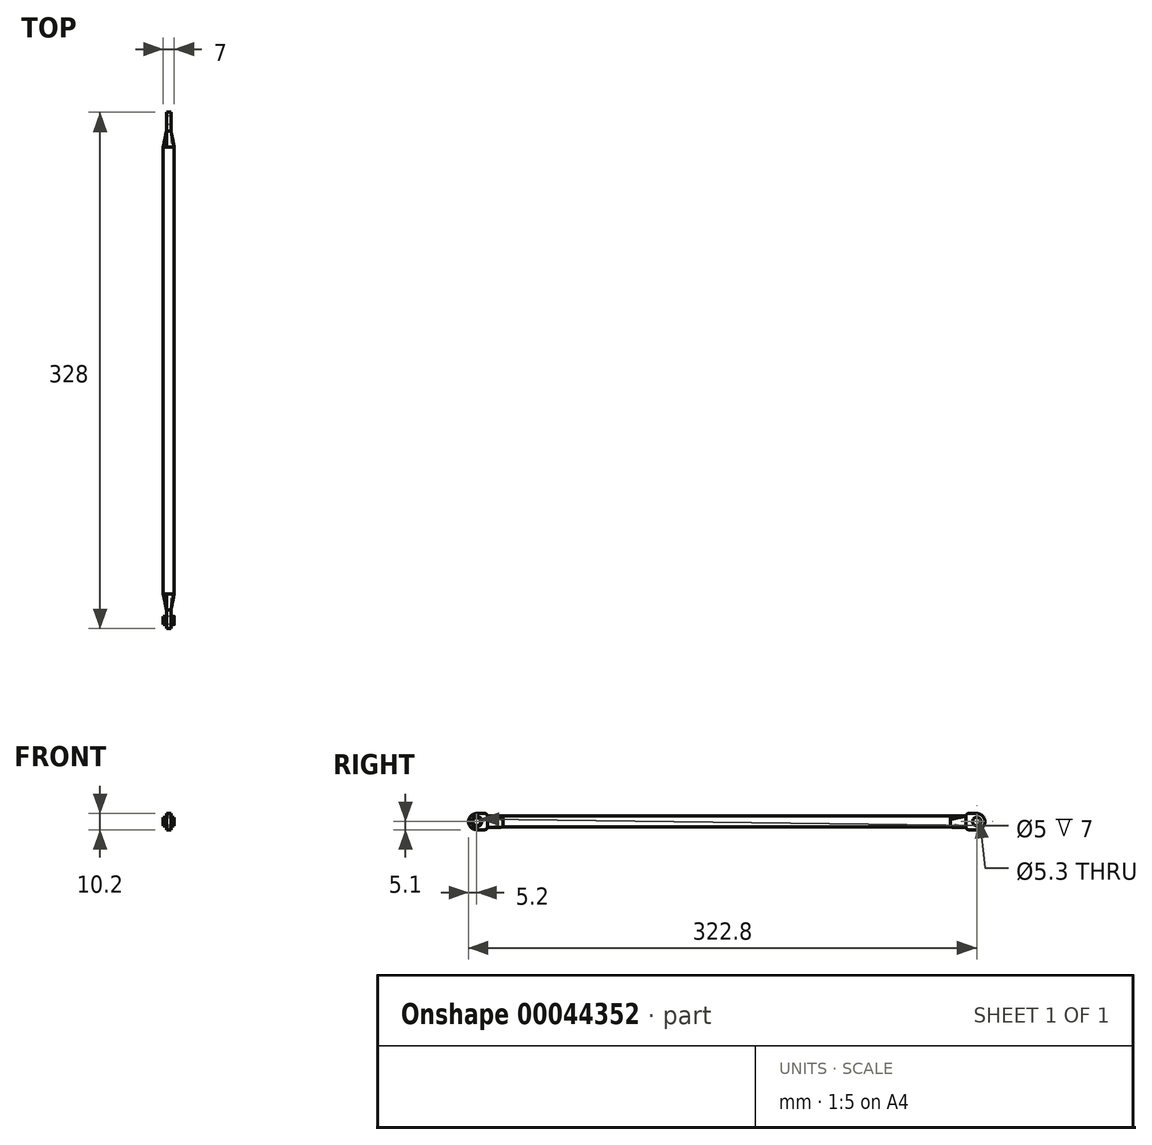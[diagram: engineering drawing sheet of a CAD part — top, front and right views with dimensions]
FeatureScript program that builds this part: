
annotation { "Feature Type Name" : "Feature", "Feature Type Description" : "" }
export const myFeature = defineFeature(function(context is Context, id is Id, definition is map)
    precondition{}
    {
        {
            var Q0;
            Q0=qCreatedBy(makeId("Right.planeOp"),FACE);
            var sketch = newSketch(context, id + "F0", { "sketchPlane" : qUnion([Q0])});
            skLineSegment(sketch, "E0.bottom", {"start": v(-0.9, 5.1) * mm, "end": v(4.5, 5.1) * mm});
            skLineSegment(sketch, "E0.top", {"start": v(-0.9, -5.1) * mm, "end": v(4.5, -5.1) * mm});
            skLineSegment(sketch, "E0.left", {"start": v(-6, 0) * mm, "end": v(-6, 0) * mm});
            skLineSegment(sketch, "E0.right", {"start": v(6, 3.6) * mm, "end": v(6, -3.6) * mm});
            skPoint(sketch, "E1.visualSharp", {"position": v(-6, 5.1) * mm});
            skArc(sketch, "E1.filletArc", {"start": v(-0.9, 5.1) * mm, "mid": v(-4.5, 3.6) * mm, "end": v(-6, 0) * mm});
            skPoint(sketch, "E2.visualSharp", {"position": v(-6, -5.1) * mm});
            skArc(sketch, "E2.filletArc", {"start": v(-6, 0) * mm, "mid": v(-4.5, -3.6) * mm, "end": v(-0.9, -5.1) * mm});
            skPoint(sketch, "E3.visualSharp", {"position": v(6, 5.1) * mm});
            skArc(sketch, "E3.filletArc", {"start": v(6, 3.6) * mm, "mid": v(5.56, 4.66) * mm, "end": v(4.5, 5.1) * mm});
            skPoint(sketch, "E4.visualSharp", {"position": v(6, -5.1) * mm});
            skArc(sketch, "E4.filletArc", {"start": v(4.5, -5.1) * mm, "mid": v(5.56, -4.66) * mm, "end": v(6, -3.6) * mm});
            skSolve(sketch);
        }
        {
            var Q0;
            Q0=makeQuery(id+"F0.imprint","IMPRINT",FACE,{"disambiguationData":[TD([[makeQuery(id+"F0.imprint","IMPRINT",EDGE,{"derivedFrom":sQuery(id+"F0.wireOp",EDGE,"E0.bottom")}),-1.0]])]});
            extrude(context, id + "F1", {"entities" : qUnion([Q0]), "endBound" : BoundingType.SYMMETRIC, "depth" : 3 * mm});
        }
        {
            var Q0;
            Q0=makeQuery(id+"F1.opExtrude","SWEPT_FACE",FACE,{"disambiguationData":[OSD([sQuery(id+"F0.wireOp",EDGE,"E0.right")])]});
            var sketch = newSketch(context, id + "F2", { "sketchPlane" : qUnion([Q0])});
            skLineSegment(sketch, "E5.bottom", {"start": v(-1.5, -3.6) * mm, "end": v(1.5, -3.6) * mm});
            skLineSegment(sketch, "E5.top", {"start": v(-1.5, 3.6) * mm, "end": v(1.5, 3.6) * mm});
            skLineSegment(sketch, "E5.left", {"start": v(-1.5, -3.6) * mm, "end": v(-1.5, 3.6) * mm});
            skLineSegment(sketch, "E5.right", {"start": v(1.5, -3.6) * mm, "end": v(1.5, 3.6) * mm});
            skSolve(sketch);
        }
        {
            var Q0;
            Q0=makeQuery(id+"F2.imprint","IMPRINT",FACE,{"disambiguationData":[TD([[makeQuery(id+"F2.imprint","IMPRINT",EDGE,{"derivedFrom":sQuery(id+"F2.wireOp",EDGE,"E5.bottom")}),1.0]])]});
            cPlane(context, id + "F3", {"entities" : qUnion([Q0]), "cplaneType" : CPlaneType.OFFSET, "offset" : 10 * mm, "width" : 150 * mm, "height" : 150 * mm});
        }
        {
            var Q0;
            Q0=qCreatedBy(id+"F3.planeOp",FACE);
            var sketch = newSketch(context, id + "F4", { "sketchPlane" : qUnion([Q0])});
            skCircle(sketch, "E6", {"center": v(0, 0) * mm, "radius": 3.5 * mm});
            skSolve(sketch);
        }
        {
            var Q1;
            Q1=qSketchRegion(id+"F2",true);
            var Q2;
            Q2=makeQuery(id+"F4.imprint","IMPRINT",FACE,{"disambiguationData":[TD([[makeQuery(id+"F4.imprint","IMPRINT",EDGE,{"derivedFrom":sQuery(id+"F4.wireOp",EDGE,"E6")}),1.0]])]});
            loft(context, id + "F5", {"operationType" : NewBodyOperationType.ADD, "sheetProfilesArray" : [{ "sheetProfileEntities" : qUnion([Q1]) }, { "sheetProfileEntities" : qUnion([Q2]) }]});
        }
        {
            var Q0;
            Q0=qSketchRegion(id+"F4",true);
            extrude(context, id + "F6", {"entities" : qUnion([Q0]), "operationType" : NewBodyOperationType.ADD, "depth" : 142 * mm});
        }
        {
            var Q0;
            Q0=qCreatedBy(makeId("Right.planeOp"),FACE);
            var sketch = newSketch(context, id + "F7", { "sketchPlane" : qUnion([Q0])});
            skCircle(sketch, "E7", {"center": v(-0.8, 0) * mm, "radius": 2.65 * mm});
            skSolve(sketch);
        }
        {
            var Q0;
            Q0=qSketchRegion(id+"F7",true);
            extrude(context, id + "F8", {"entities" : qUnion([Q0]), "endBound" : BoundingType.SYMMETRIC, "depth" : 7 * mm});
        }
        {
            var Q0;
            Q0=qCreatedBy(makeId("Right.planeOp"),FACE);
            var sketch = newSketch(context, id + "F9", { "sketchPlane" : qUnion([Q0])});
            skLineSegment(sketch, "E8", {"start": v(-3.45, 0) * mm, "end": v(1.85, 0) * mm, "construction": true});
            skArc(sketch, "E9", {"start": v(-4.4, 0) * mm, "mid": v(-0.8, 3.6) * mm, "end": v(2.8, 0) * mm});
            skPoint(sketch, "E9.startSnap0", {"position": v(-0.8, 0) * mm});
            skLineSegment(sketch, "E10", {"start": v(-4.4, 0) * mm, "end": v(2.8, 0) * mm});
            skSolve(sketch);
        }
        {
            var Q0;
            Q0=qSketchRegion(id+"F9",true);
            var Q1;
            Q1=sQuery(id+"F9.wireOp",EDGE,"E10");
            revolve(context, id + "F10", {"entities" : qUnion([Q0]), "axis" : qUnion([Q1]), "revolveType" : RevolveType.FULL});
        }
        {
            var Q0;
            Q0=makeQuery(id+"F8.opExtrude","SWEPT_BODY",BODY,{"disambiguationData":[OSD([sQuery(id+"F7.wireOp",EDGE,"E7")])]});
            var Q1;
            Q1=makeQuery(id+"F1.opExtrude","SWEPT_BODY",BODY,{"disambiguationData":[OSD([sQuery(id+"F0.wireOp",EDGE,"E0.bottom"),sQuery(id+"F0.wireOp",EDGE,"E0.top"),sQuery(id+"F0.wireOp",EDGE,"E0.right"),sQuery(id+"F0.wireOp",EDGE,"E1.filletArc"),sQuery(id+"F0.wireOp",EDGE,"E2.filletArc"),sQuery(id+"F0.wireOp",EDGE,"E3.filletArc"),sQuery(id+"F0.wireOp",EDGE,"E4.filletArc")])]});
            booleanBodies(context, id + "F11", {"operationType" : BooleanOperationType.SUBTRACTION, "tools" : qUnion([Q0]), "targets" : qUnion([Q1]), "keepTools" : true});
        }
        {
            var Q0;
            Q0=qCreatedBy(makeId("Right.planeOp"),FACE);
            var sketch = newSketch(context, id + "F12", { "sketchPlane" : qUnion([Q0])});
            skCircle(sketch, "E11", {"center": v(-0.8, 0) * mm, "radius": 2.5 * mm});
            skSolve(sketch);
        }
        {
            var Q0;
            Q0=qSketchRegion(id+"F12",true);
            extrude(context, id + "F13", {"entities" : qUnion([Q0]), "operationType" : NewBodyOperationType.REMOVE, "endBound" : BoundingType.SYMMETRIC, "depth" : 10 * mm});
        }
        {
            var Q0;
            Q0=makeQuery(id+"F6.opExtrude","CAP_FACE",FACE,{"disambiguationData":[OSD([sQuery(id+"F4.wireOp",EDGE,"E6")])],"isStart":false});
            cPlane(context, id + "F14", {"entities" : qUnion([Q0]), "cplaneType" : CPlaneType.OFFSET, "offset" : 0 * mm, "width" : 150 * mm, "height" : 150 * mm});
        }
        {
            var Q0;
            Q0=makeQuery(id+"F1.opExtrude","SWEPT_BODY",BODY,{"disambiguationData":[OSD([sQuery(id+"F0.wireOp",EDGE,"E0.bottom"),sQuery(id+"F0.wireOp",EDGE,"E0.top"),sQuery(id+"F0.wireOp",EDGE,"E0.right"),sQuery(id+"F0.wireOp",EDGE,"E1.filletArc"),sQuery(id+"F0.wireOp",EDGE,"E2.filletArc"),sQuery(id+"F0.wireOp",EDGE,"E3.filletArc"),sQuery(id+"F0.wireOp",EDGE,"E4.filletArc")])]});
            var Q1;
            Q1=qCreatedBy(id+"F14.planeOp",FACE);
            mirror(context, id + "F15", {"operationType" : NewBodyOperationType.ADD, "entities" : qUnion([Q0]), "mirrorPlane" : qUnion([Q1])});
        }
    });
